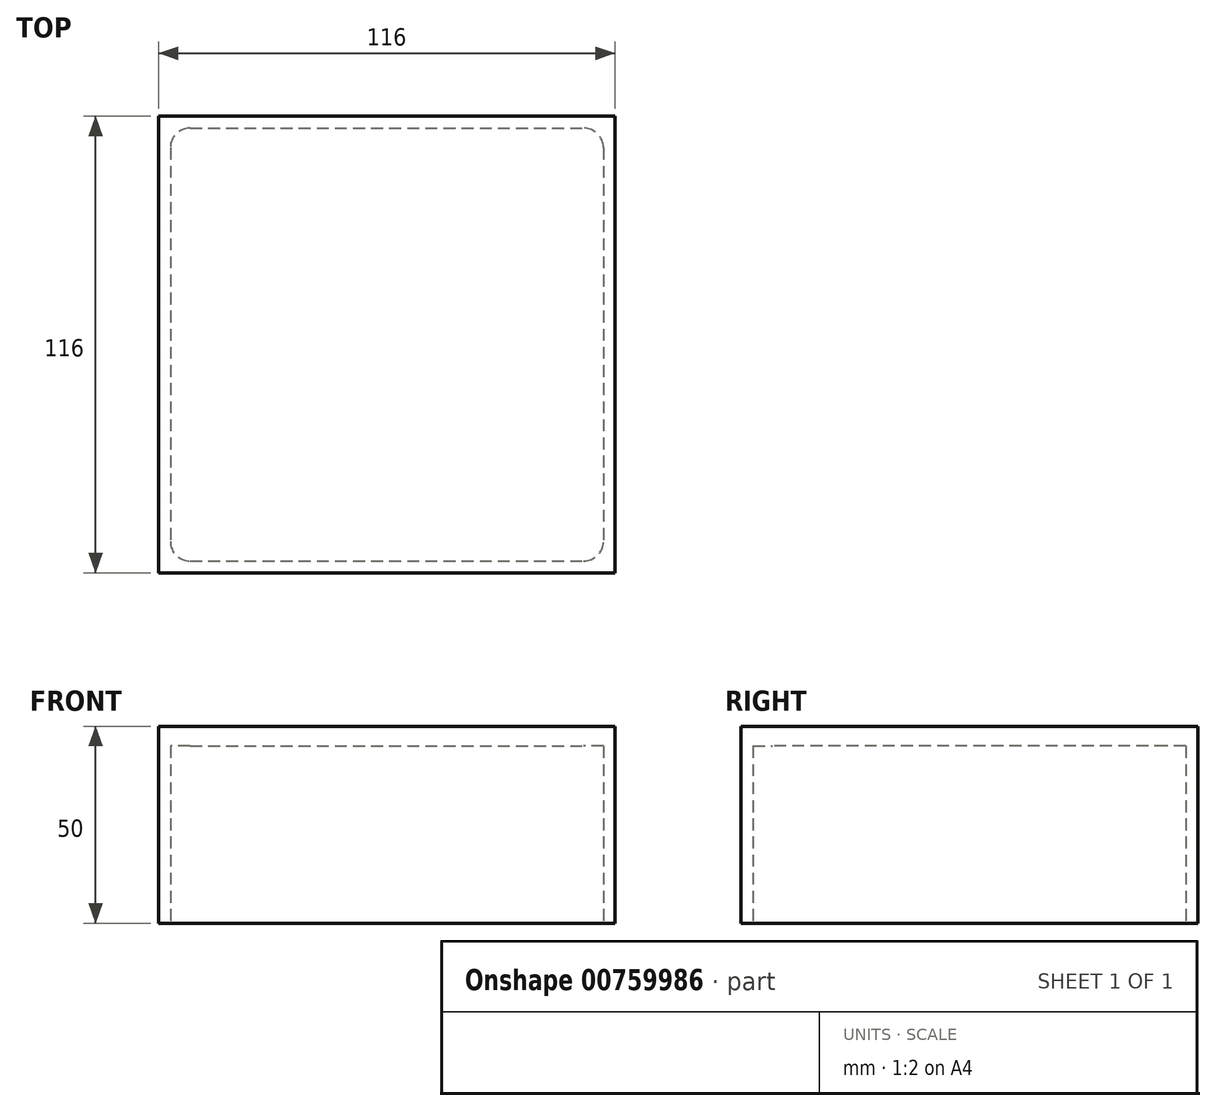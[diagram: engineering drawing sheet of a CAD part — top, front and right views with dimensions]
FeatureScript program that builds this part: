
annotation { "Feature Type Name" : "Feature", "Feature Type Description" : "" }
export const myFeature = defineFeature(function(context is Context, id is Id, definition is map)
    precondition{}
    {
        {
            var Q0;
            Q0=qCreatedBy(makeId("Top.planeOp"),FACE);
            var sketch = newSketch(context, id + "F0", { "sketchPlane" : qUnion([Q0])});
            skLineSegment(sketch, "E0.bottom", {"start": v(-58, 58) * mm, "end": v(58, 58) * mm});
            skLineSegment(sketch, "E0.top", {"start": v(-58, -58) * mm, "end": v(58, -58) * mm});
            skLineSegment(sketch, "E0.left", {"start": v(-58, 58) * mm, "end": v(-58, -58) * mm});
            skLineSegment(sketch, "E0.right", {"start": v(58, 58) * mm, "end": v(58, -58) * mm});
            skPoint(sketch, "E0.middle", {"position": v(0, 0) * mm});
            skSolve(sketch);
        }
        {
            var Q0;
            Q0=qSketchRegion(id+"F0",true);
            extrude(context, id + "F1", {"entities" : qUnion([Q0]), "depth" : 50 * mm, "offsetDistance" : 25 * mm});
        }
        {
            var Q0;
            Q0=qCreatedBy(makeId("Top.planeOp"),FACE);
            var sketch = newSketch(context, id + "F2", { "sketchPlane" : qUnion([Q0])});
            skLineSegment(sketch, "E1.bottom", {"start": v(-55, 55) * mm, "end": v(55, 55) * mm});
            skLineSegment(sketch, "E1.top", {"start": v(-55, -55) * mm, "end": v(55, -55) * mm});
            skLineSegment(sketch, "E1.left", {"start": v(-55, 55) * mm, "end": v(-55, -55) * mm});
            skLineSegment(sketch, "E1.right", {"start": v(55, 55) * mm, "end": v(55, -55) * mm});
            skPoint(sketch, "E1.middle", {"position": v(0, 0) * mm});
            skSolve(sketch);
        }
        {
            var Q0;
            Q0=qSketchRegion(id+"F2",true);
            extrude(context, id + "F3", {"entities" : qUnion([Q0]), "operationType" : NewBodyOperationType.REMOVE, "depth" : 45 * mm, "offsetDistance" : 25 * mm});
        }
        {
            var Q0;
            Q0=makeQuery(id+"F3.boolean.opBoolean","COPY",EDGE,{"derivedFrom":makeQuery(id+"F3.opExtrude","SWEPT_EDGE",EDGE,{"disambiguationData":[OSD([sQuery(id+"F2.wireOp",EDGE,"E1.bottom"),sQuery(id+"F2.wireOp",EDGE,"E1.right")])]})});
            var Q1;
            Q1=makeQuery(id+"F3.boolean.opBoolean","COPY",EDGE,{"derivedFrom":makeQuery(id+"F3.opExtrude","SWEPT_EDGE",EDGE,{"disambiguationData":[OSD([sQuery(id+"F2.wireOp",EDGE,"E1.top"),sQuery(id+"F2.wireOp",EDGE,"E1.left")])]})});
            var Q2;
            Q2=makeQuery(id+"F3.boolean.opBoolean","COPY",EDGE,{"derivedFrom":makeQuery(id+"F3.opExtrude","SWEPT_EDGE",EDGE,{"disambiguationData":[OSD([sQuery(id+"F2.wireOp",EDGE,"E1.top"),sQuery(id+"F2.wireOp",EDGE,"E1.right")])]})});
            var Q3;
            Q3=makeQuery(id+"F3.boolean.opBoolean","COPY",EDGE,{"derivedFrom":makeQuery(id+"F3.opExtrude","SWEPT_EDGE",EDGE,{"disambiguationData":[OSD([sQuery(id+"F2.wireOp",EDGE,"E1.bottom"),sQuery(id+"F2.wireOp",EDGE,"E1.left")])]})});
            fillet(context, id + "F4", {"entities" : qUnion([Q0, Q1, Q2, Q3]), "radius" : 5 * mm, "tangentPropagation" : true, "allowEdgeOverflow" : false});
        }
    });
